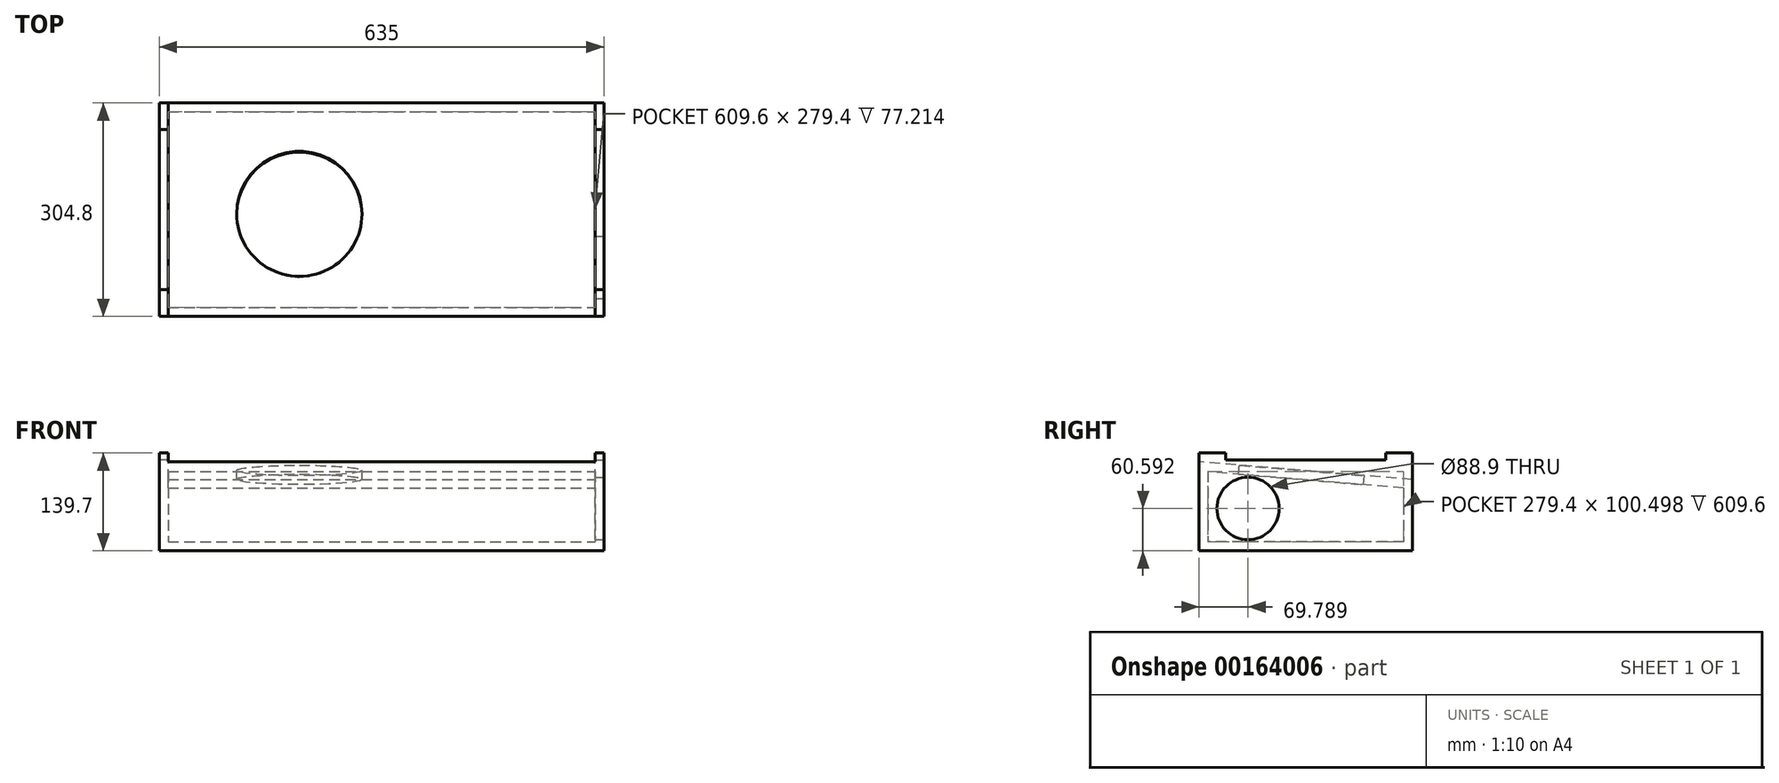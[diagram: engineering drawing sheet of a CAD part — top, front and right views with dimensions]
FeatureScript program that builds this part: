
annotation { "Feature Type Name" : "Feature", "Feature Type Description" : "" }
export const myFeature = defineFeature(function(context is Context, id is Id, definition is map)
    precondition{}
    {
        {
            var Q0;
            Q0=qCreatedBy(makeId("Top.planeOp"),FACE);
            var sketch = newSketch(context, id + "F0", { "sketchPlane" : qUnion([Q0])});
            skLineSegment(sketch, "E0.bottom", {"start": v(-317.5, 152.4) * mm, "end": v(317.5, 152.4) * mm});
            skLineSegment(sketch, "E0.top", {"start": v(-317.5, -152.4) * mm, "end": v(317.5, -152.4) * mm});
            skLineSegment(sketch, "E0.left", {"start": v(-317.5, 152.4) * mm, "end": v(-317.5, -152.4) * mm});
            skLineSegment(sketch, "E0.right", {"start": v(317.5, 152.4) * mm, "end": v(317.5, -152.4) * mm});
            skPoint(sketch, "E0.middle", {"position": v(0, 0) * mm});
            skSolve(sketch);
        }
        {
            var Q0;
            Q0=makeQuery(id+"F0.imprint","IMPRINT",FACE,{"disambiguationData":[TD([[makeQuery(id+"F0.imprint","IMPRINT",EDGE,{"derivedFrom":sQuery(id+"F0.wireOp",EDGE,"E0.bottom")}),-1.0]])]});
            extrude(context, id + "F1", {"entities" : qUnion([Q0]), "depth" : 127 * mm});
        }
        {
            var Q0;
            Q0=makeQuery(id+"F1.opExtrude","SWEPT_FACE",FACE,{"disambiguationData":[OSD([sQuery(id+"F0.wireOp",EDGE,"E0.right")])]});
            var sketch = newSketch(context, id + "F2", { "sketchPlane" : qUnion([Q0])});
            skLineSegment(sketch, "E1", {"start": v(152.4, 0) * mm, "end": v(152.4, 101.6) * mm});
            skLineSegment(sketch, "E2", {"start": v(152.4, 101.6) * mm, "end": v(-152.4, 127) * mm});
            skSolve(sketch);
        }
        {
            var Q0;
            {var subQ0=sQuery(id+"F2.wireOp",EDGE,"E2");Q0=makeQuery(id+"F2.imprint","IMPRINT",FACE,{"disambiguationData":[TD([[makeQuery(id+"F2.imprint","IMPRINT",EDGE,{"derivedFrom":subQ0}),-1.0]])]});}
            extrude(context, id + "F3", {"entities" : qUnion([Q0]), "operationType" : NewBodyOperationType.REMOVE, "endBound" : BoundingType.THROUGH_ALL, "oppositeDirection" : true, "depth" : 25.4 * mm});
        }
        {
            var Q0;
            Q0=makeQuery(id+"F1.opExtrude","SWEPT_FACE",FACE,{"disambiguationData":[OSD([sQuery(id+"F0.wireOp",EDGE,"E0.top")])]});
            var Q1;
            Q1=makeQuery(id+"F1.opExtrude","SWEPT_FACE",FACE,{"disambiguationData":[OSD([sQuery(id+"F0.wireOp",EDGE,"E0.left")])]});
            var Q2;
            Q2=makeQuery(id+"F1.opExtrude","CAP_FACE",FACE,{"disambiguationData":[OSD([sQuery(id+"F0.wireOp",EDGE,"E0.bottom"),sQuery(id+"F0.wireOp",EDGE,"E0.top"),sQuery(id+"F0.wireOp",EDGE,"E0.left"),sQuery(id+"F0.wireOp",EDGE,"E0.right")])],"isStart":true});
            var Q3;
            Q3=makeQuery(id+"F1.opExtrude","SWEPT_FACE",FACE,{"disambiguationData":[OSD([sQuery(id+"F0.wireOp",EDGE,"E0.right")])]});
            var Q4;
            Q4=makeQuery(id+"F1.opExtrude","SWEPT_FACE",FACE,{"disambiguationData":[OSD([sQuery(id+"F0.wireOp",EDGE,"E0.bottom")])]});
            var Q5;
            Q5=makeQuery(id+"F3.boolean.opBoolean","COPY",FACE,{"derivedFrom":makeQuery(id+"F3.opExtrude","SWEPT_FACE",FACE,{"disambiguationData":[OSD([sQuery(id+"F2.wireOp",EDGE,"E2")])]})});
            var Q6;
            Q6=makeQuery(id+"F1.opExtrude","SWEPT_BODY",BODY,{"disambiguationData":[OSD([sQuery(id+"F0.wireOp",EDGE,"E0.bottom"),sQuery(id+"F0.wireOp",EDGE,"E0.top"),sQuery(id+"F0.wireOp",EDGE,"E0.left"),sQuery(id+"F0.wireOp",EDGE,"E0.right")])]});
            shell(context, id + "F4", {"isHollow" : true, "entities" : qUnion([Q0, Q1, Q2, Q3, Q4, Q5]), "parts" : qUnion([Q6]), "thickness" : 12.7 * mm});
        }
        {
            var Q0;
            Q0=makeQuery(id+"F3.boolean.opBoolean","COPY",FACE,{"derivedFrom":makeQuery(id+"F3.opExtrude","SWEPT_FACE",FACE,{"disambiguationData":[OSD([sQuery(id+"F2.wireOp",EDGE,"E2")])]})});
            var sketch = newSketch(context, id + "F5", { "sketchPlane" : qUnion([Q0])});
            skCircle(sketch, "E3", {"center": v(-117.47, -15.31) * mm, "radius": 89.53 * mm});
            skSolve(sketch);
        }
        {
            var Q0;
            Q0=makeQuery(id+"F5.imprint","IMPRINT",FACE,{"disambiguationData":[TD([[makeQuery(id+"F5.imprint","IMPRINT",EDGE,{"derivedFrom":sQuery(id+"F5.wireOp",EDGE,"E3")}),1.0]])]});
            extrude(context, id + "F6", {"entities" : qUnion([Q0]), "operationType" : NewBodyOperationType.REMOVE, "endBound" : BoundingType.UP_TO_NEXT, "oppositeDirection" : true, "depth" : 25.4 * mm});
        }
        {
            var Q0;
            Q0=makeQuery(id+"F2.imprint","IMPRINT",FACE,{"disambiguationData":[TD([[makeQuery(id+"F2.imprint","IMPRINT",EDGE,{"derivedFrom":sQuery(id+"F2.wireOp",EDGE,"E1")}),-1.0]])]});
            var sketch = newSketch(context, id + "F7", { "sketchPlane" : qUnion([Q0])});
            skLineSegment(sketch, "E4", {"start": v(152.4, 50.8) * mm, "end": v(-152.4, 63.5) * mm, "construction": true});
            skCircle(sketch, "E5", {"center": v(-82.61, 60.6) * mm, "radius": 44.45 * mm});
            skSolve(sketch);
        }
        {
            var Q0;
            Q0=sQuery(id+"F7.wireOp",VERTEX,"E5.center");
            var Q1;
            Q1=makeQuery(id+"F1.opExtrude","SWEPT_BODY",BODY,{"disambiguationData":[OSD([sQuery(id+"F0.wireOp",EDGE,"E0.bottom"),sQuery(id+"F0.wireOp",EDGE,"E0.top"),sQuery(id+"F0.wireOp",EDGE,"E0.left"),sQuery(id+"F0.wireOp",EDGE,"E0.right")])]});
            hole(context, id + "F8", {"style" : HoleStyle.SIMPLE, "endStyle" : HoleEndStyle.BLIND, "holeDiameter" : 88.9 * mm, "holeDepth" : 25.4 * mm, "locations" : qUnion([Q0]), "scope" : qUnion([Q1])});
        }
        {
            var Q0;
            Q0=makeQuery(id+"F2.imprint","IMPRINT",FACE,{"disambiguationData":[TD([[makeQuery(id+"F2.imprint","IMPRINT",EDGE,{"derivedFrom":sQuery(id+"F2.wireOp",EDGE,"E1")}),-1.0]])]});
            var sketch = newSketch(context, id + "F9", { "sketchPlane" : qUnion([Q0])});
            skLineSegment(sketch, "E6", {"start": v(-152.4, 0) * mm, "end": v(152.4, 0) * mm});
            skLineSegment(sketch, "E7", {"start": v(152.4, 0) * mm, "end": v(152.4, 139.7) * mm});
            skLineSegment(sketch, "E8", {"start": v(152.4, 139.7) * mm, "end": v(114.3, 139.7) * mm});
            skLineSegment(sketch, "E9", {"start": v(-152.4, 139.7) * mm, "end": v(-152.4, 0) * mm});
            skLineSegment(sketch, "E10", {"start": v(-114.3, 139.7) * mm, "end": v(-114.3, 130.1) * mm});
            skLineSegment(sketch, "E11", {"start": v(-114.3, 130.1) * mm, "end": v(114.3, 130.1) * mm});
            skLineSegment(sketch, "E12", {"start": v(114.3, 130.1) * mm, "end": v(114.3, 139.7) * mm});
            skLineSegment(sketch, "E13.trimOffspring", {"start": v(-114.3, 139.7) * mm, "end": v(-152.4, 139.7) * mm});
            skSolve(sketch);
        }
        {
            var Q0;
            {var subQ3=sQuery(id+"F9.wireOp",EDGE,"E8");Q0=makeQuery(id+"F9.imprint","IMPRINT",FACE,{"disambiguationData":[TD([[makeQuery(id+"F9.imprint","IMPRINT",EDGE,{"derivedFrom":subQ3}),1.0]])]});}
            extrude(context, id + "F10", {"entities" : qUnion([Q0]), "operationType" : NewBodyOperationType.ADD, "oppositeDirection" : true, "depth" : 12.7 * mm});
        }
        {
            var Q0;
            Q0=makeQuery(id+"F1.opExtrude","SWEPT_FACE",FACE,{"disambiguationData":[OSD([sQuery(id+"F0.wireOp",EDGE,"E0.left")])]});
            var sketch = newSketch(context, id + "F11", { "sketchPlane" : qUnion([Q0])});
            skLineSegment(sketch, "E14", {"start": v(-152.4, 101.6) * mm, "end": v(-152.4, 139.7) * mm});
            skLineSegment(sketch, "E15", {"start": v(-152.4, 139.7) * mm, "end": v(-114.3, 139.7) * mm});
            skLineSegment(sketch, "E16", {"start": v(-114.3, 139.7) * mm, "end": v(-114.3, 130.1) * mm});
            skLineSegment(sketch, "E17", {"start": v(-114.3, 130.1) * mm, "end": v(114.3, 130.1) * mm});
            skLineSegment(sketch, "E18", {"start": v(114.3, 130.1) * mm, "end": v(114.3, 139.7) * mm});
            skLineSegment(sketch, "E19", {"start": v(114.3, 139.7) * mm, "end": v(152.4, 139.7) * mm});
            skLineSegment(sketch, "E20", {"start": v(152.4, 139.7) * mm, "end": v(152.4, 127) * mm});
            skSolve(sketch);
        }
        {
            var Q0;
            Q0=makeQuery(id+"F11.imprint","IMPRINT",FACE,{"disambiguationData":[TD([[makeQuery(id+"F11.imprint","IMPRINT",EDGE,{"derivedFrom":sQuery(id+"F11.wireOp",EDGE,"E14")}),-1.0]])]});
            extrude(context, id + "F12", {"entities" : qUnion([Q0]), "operationType" : NewBodyOperationType.ADD, "oppositeDirection" : true, "depth" : 12.7 * mm});
        }
    });
